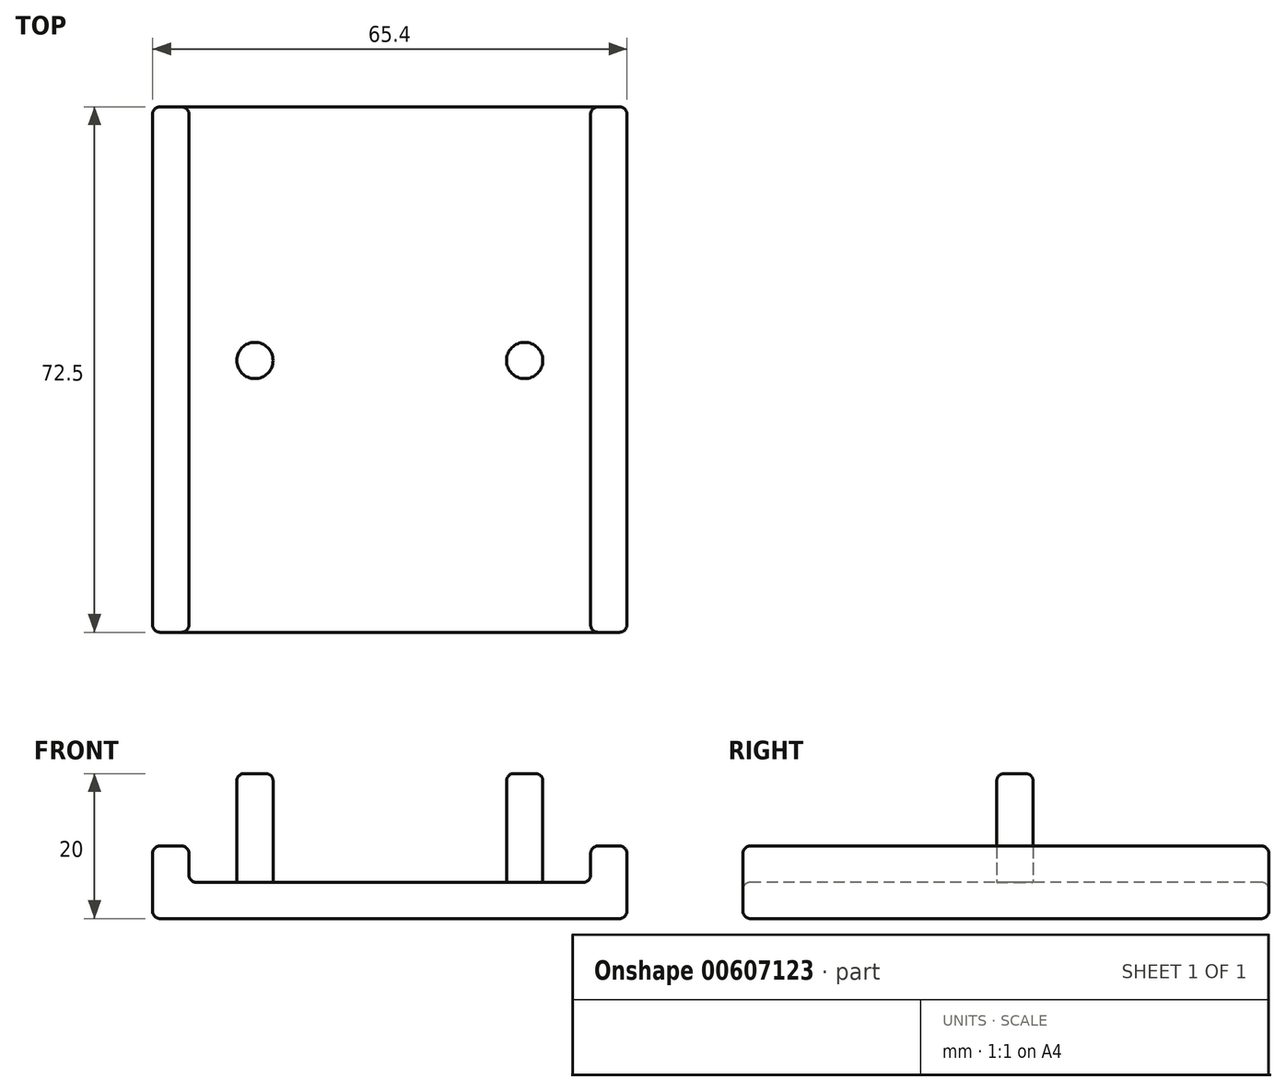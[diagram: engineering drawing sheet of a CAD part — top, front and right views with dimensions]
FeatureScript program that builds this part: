
annotation { "Feature Type Name" : "Feature", "Feature Type Description" : "" }
export const myFeature = defineFeature(function(context is Context, id is Id, definition is map)
    precondition{}
    {
        {
            var Q0;
            Q0=qCreatedBy(makeId("Front.planeOp"),FACE);
            var sketch = newSketch(context, id + "F0", { "sketchPlane" : qUnion([Q0])});
            skLineSegment(sketch, "E0", {"start": v(0, 0) * mm, "end": v(-32.7, 0) * mm});
            skLineSegment(sketch, "E1", {"start": v(-32.7, 0) * mm, "end": v(-32.7, 10) * mm});
            skLineSegment(sketch, "E2", {"start": v(-32.7, 10) * mm, "end": v(-27.7, 10) * mm});
            skLineSegment(sketch, "E3", {"start": v(-27.7, 10) * mm, "end": v(-27.7, 5) * mm});
            skLineSegment(sketch, "E4", {"start": v(-27.7, 5) * mm, "end": v(0, 5) * mm});
            skLineSegment(sketch, "E5.MirrorCS", {"start": v(0, 0) * mm, "end": v(32.7, 0) * mm});
            skLineSegment(sketch, "E6.MirrorCS", {"start": v(32.7, 10) * mm, "end": v(27.7, 10) * mm});
            skLineSegment(sketch, "E7.MirrorCS", {"start": v(27.7, 5) * mm, "end": v(0, 5) * mm});
            skLineSegment(sketch, "E8.MirrorCS", {"start": v(32.7, 0) * mm, "end": v(32.7, 10) * mm});
            skLineSegment(sketch, "E9.MirrorCS", {"start": v(27.7, 10) * mm, "end": v(27.7, 5) * mm});
            skSolve(sketch);
        }
        {
            var Q0;
            Q0 = qSketchRegion(id + "F0", true);
            extrude(context, id + "F1", {"entities" : qUnion([Q0]), "oppositeDirection" : true, "depth" : 35 * mm, "offsetDistance" : 25 * mm, "hasSecondDirection" : true, "secondDirectionOppositeDirection" : false, "secondDirectionDepth" : 37.5 * mm});
        }
        {
            var Q0;
            Q0=makeQuery(id+"F1.opExtrude","SWEPT_FACE",FACE,{"disambiguationData":[OSD([sQuery(id+"F0.wireOp",EDGE,"E4"),sQuery(id+"F0.wireOp",EDGE,"E7.MirrorCS")])]});
            var sketch = newSketch(context, id + "F2", { "sketchPlane" : qUnion([Q0])});
            skCircle(sketch, "E10", {"center": v(-18.6, 0) * mm, "radius": 2.5 * mm});
            skCircle(sketch, "E11", {"center": v(18.6, 0) * mm, "radius": 2.5 * mm});
            skSolve(sketch);
        }
        {
            var Q0;
            Q0 = qSketchRegion(id + "F2", true);
            extrude(context, id + "F3", {"entities" : qUnion([Q0]), "operationType" : NewBodyOperationType.ADD, "depth" : 15 * mm, "offsetDistance" : 25 * mm});
        }
        {
            var Q0;
            Q0=makeQuery(id+"F1.opExtrude","SWEPT_EDGE",EDGE,{"disambiguationData":[OSD([sQuery(id+"F0.wireOp",EDGE,"E3"),sQuery(id+"F0.wireOp",EDGE,"E4")])]});
            var Q1;
            Q1=makeQuery(id+"F1.opExtrude","SWEPT_EDGE",EDGE,{"disambiguationData":[OSD([sQuery(id+"F0.wireOp",EDGE,"E7.MirrorCS"),sQuery(id+"F0.wireOp",EDGE,"E9.MirrorCS")])]});
            var Q2;
            Q2=makeQuery(id+"F1.opExtrude","SWEPT_EDGE",EDGE,{"disambiguationData":[OSD([sQuery(id+"F0.wireOp",EDGE,"E2"),sQuery(id+"F0.wireOp",EDGE,"E3")])]});
            var Q3;
            Q3=makeQuery(id+"F1.opExtrude","SWEPT_EDGE",EDGE,{"disambiguationData":[OSD([sQuery(id+"F0.wireOp",EDGE,"E1"),sQuery(id+"F0.wireOp",EDGE,"E2")])]});
            var Q4;
            Q4=makeQuery(id+"F1.opExtrude","SWEPT_EDGE",EDGE,{"disambiguationData":[OSD([sQuery(id+"F0.wireOp",EDGE,"E6.MirrorCS"),sQuery(id+"F0.wireOp",EDGE,"E9.MirrorCS")])]});
            var Q5;
            Q5=makeQuery(id+"F1.opExtrude","SWEPT_EDGE",EDGE,{"disambiguationData":[OSD([sQuery(id+"F0.wireOp",EDGE,"E6.MirrorCS"),sQuery(id+"F0.wireOp",EDGE,"E8.MirrorCS")])]});
            var Q6;
            Q6=makeQuery(id+"F1.opExtrude","SWEPT_EDGE",EDGE,{"disambiguationData":[OSD([sQuery(id+"F0.wireOp",EDGE,"E5.MirrorCS"),sQuery(id+"F0.wireOp",EDGE,"E8.MirrorCS")])]});
            var Q7;
            Q7=makeQuery(id+"F1.opExtrude","SWEPT_EDGE",EDGE,{"disambiguationData":[OSD([sQuery(id+"F0.wireOp",EDGE,"E0"),sQuery(id+"F0.wireOp",EDGE,"E1")])]});
            fillet(context, id + "F4", {"entities" : qUnion([Q0, Q1, Q2, Q3, Q4, Q5, Q6, Q7]), "radius" : 1 * mm, "tangentPropagation" : true, "allowEdgeOverflow" : false});
        }
        {
            var Q0;
            Q0=makeQuery(id+"F3.opExtrude","CAP_EDGE",EDGE,{"disambiguationData":[OSD([sQuery(id+"F2.wireOp",EDGE,"E10")])],"isStart":false});
            var Q1;
            Q1=makeQuery(id+"F3.opExtrude","CAP_EDGE",EDGE,{"disambiguationData":[OSD([sQuery(id+"F2.wireOp",EDGE,"E11")])],"isStart":false});
            fillet(context, id + "F5", {"entities" : qUnion([Q0, Q1]), "radius" : 1 * mm, "tangentPropagation" : true, "allowEdgeOverflow" : false});
        }
        {
            var Q0;
            Q0=makeQuery(id+"F1.opExtrude","CAP_EDGE",EDGE,{"disambiguationData":[OSD([sQuery(id+"F0.wireOp",EDGE,"E4"),sQuery(id+"F0.wireOp",EDGE,"E7.MirrorCS")])],"isStart":true});
            var Q1;
            Q1=makeQuery(id+"F1.opExtrude","CAP_EDGE",EDGE,{"disambiguationData":[OSD([sQuery(id+"F0.wireOp",EDGE,"E0"),sQuery(id+"F0.wireOp",EDGE,"E5.MirrorCS")])],"isStart":false});
            var Q2;
            Q2=makeQuery(id+"F3.opExtrude","CAP_EDGE",EDGE,{"disambiguationData":[OSD([sQuery(id+"F2.wireOp",EDGE,"E10")])],"isStart":true});
            var Q3;
            Q3=makeQuery(id+"F3.opExtrude","CAP_EDGE",EDGE,{"disambiguationData":[OSD([sQuery(id+"F2.wireOp",EDGE,"E11")])],"isStart":true});
            fillet(context, id + "F6", {"entities" : qUnion([Q0, Q1, Q2, Q3]), "radius" : 1 * mm, "tangentPropagation" : true, "allowEdgeOverflow" : false});
        }
    });
